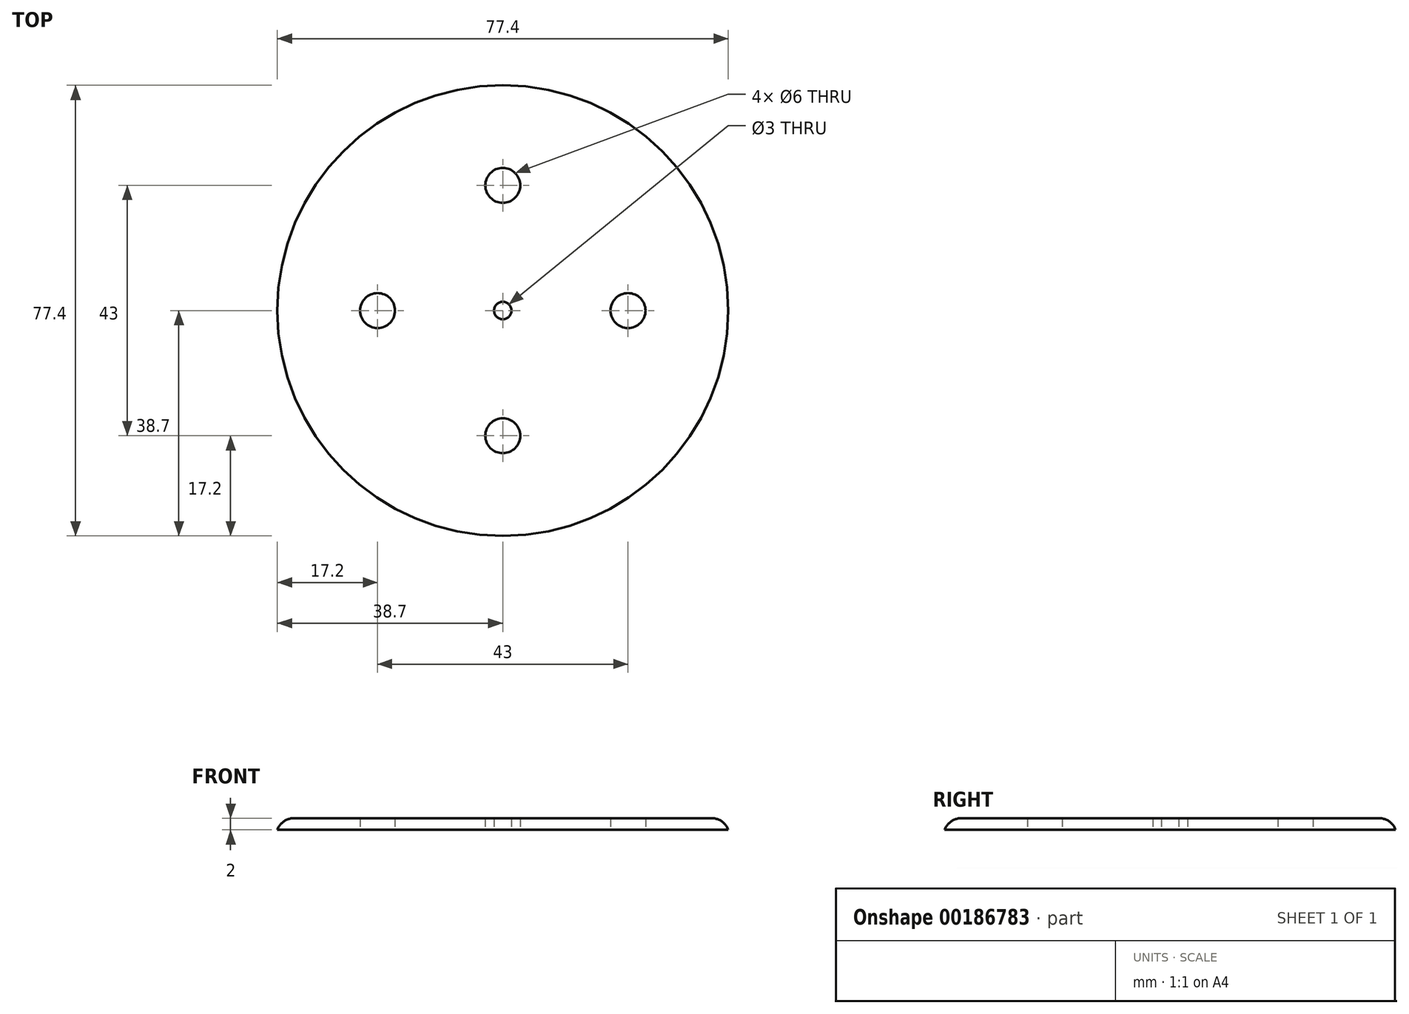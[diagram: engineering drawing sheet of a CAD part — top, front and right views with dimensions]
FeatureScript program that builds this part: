
annotation { "Feature Type Name" : "Feature", "Feature Type Description" : "" }
export const myFeature = defineFeature(function(context is Context, id is Id, definition is map)
    precondition{}
    {
        {
            var Q0;
            Q0=qCreatedBy(makeId("Top.planeOp"),FACE);
            var sketch = newSketch(context, id + "F0", { "sketchPlane" : qUnion([Q0])});
            skCircle(sketch, "E0", {"center": v(0, 0) * mm, "radius": 38.7 * mm});
            skLineSegment(sketch, "E1", {"start": v(-38.7, 0) * mm, "end": v(38.7, 0) * mm, "construction": true});
            skLineSegment(sketch, "E2", {"start": v(0, 38.7) * mm, "end": v(0, -38.7) * mm, "construction": true});
            skCircle(sketch, "E3", {"center": v(0, 21.5) * mm, "radius": 3 * mm});
            skCircle(sketch, "E4.MirrorC", {"center": v(0, -21.5) * mm, "radius": 3 * mm});
            skCircle(sketch, "E5", {"center": v(0, 0) * mm, "radius": 1.5 * mm});
            skCircle(sketch, "E6", {"center": v(-21.5, 0) * mm, "radius": 3 * mm});
            skCircle(sketch, "E7", {"center": v(21.5, 0) * mm, "radius": 3 * mm});
            skSolve(sketch);
        }
        {
            var Q0;
            Q0 = qSketchRegion(id + "F0", true);
            extrude(context, id + "F1", {"entities" : qUnion([Q0]), "depth" : 2 * mm, "offsetDistance" : 25 * mm});
        }
        {
            var Q0;
            Q0=makeQuery(id+"F1.opExtrude","CAP_EDGE",EDGE,{"disambiguationData":[OSD([sQuery(id+"F0.wireOp",EDGE,"E0")])],"isStart":false});
            fillet(context, id + "F2", {"entities" : qUnion([Q0]), "radius" : 3 * mm, "tangentPropagation" : true, "allowEdgeOverflow" : false});
        }
    });
